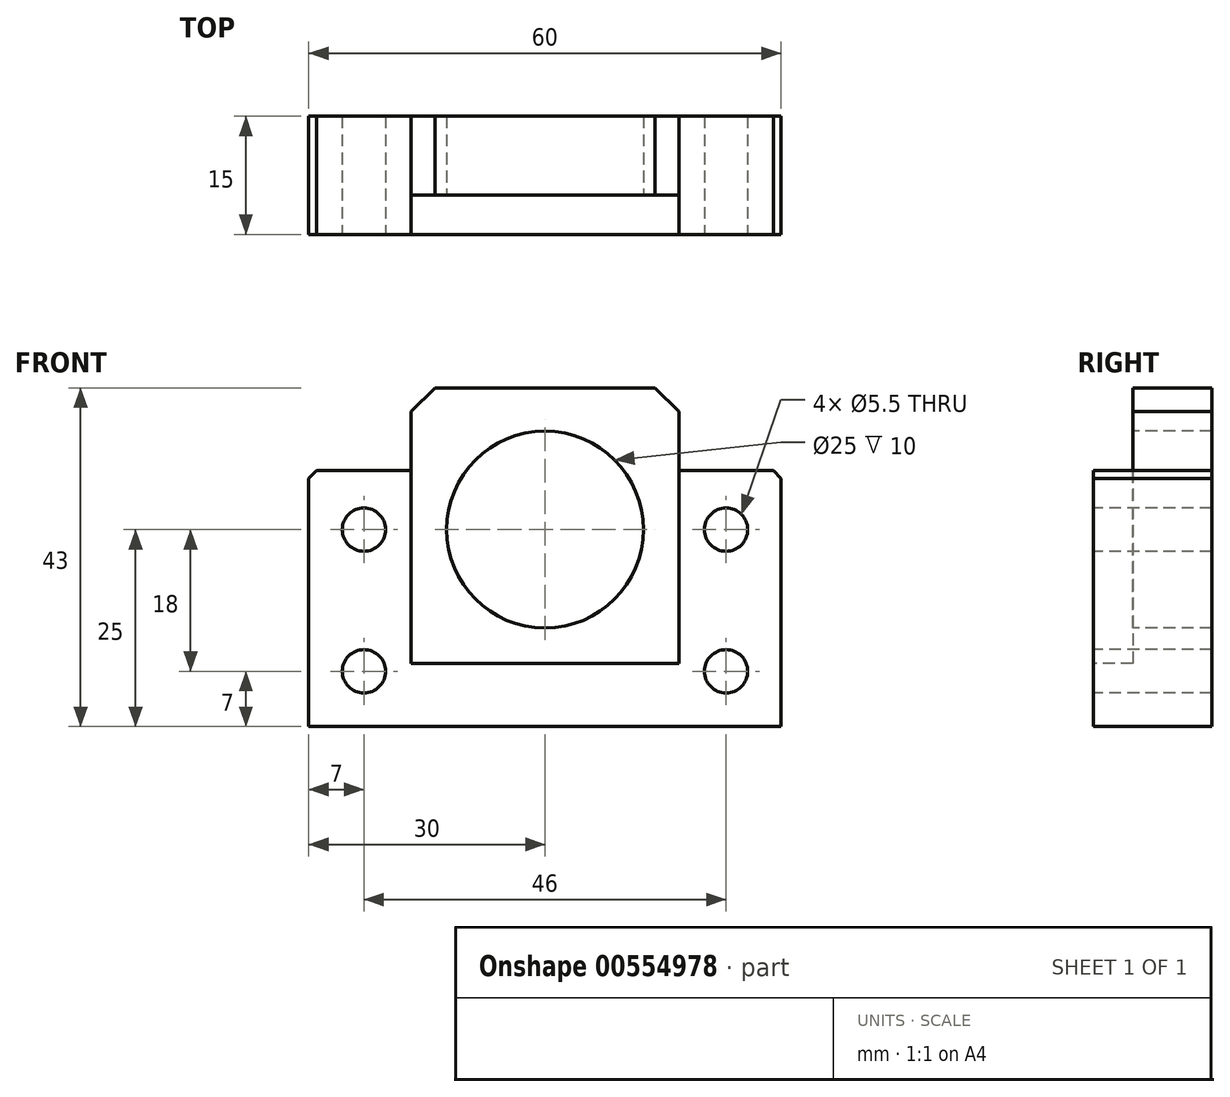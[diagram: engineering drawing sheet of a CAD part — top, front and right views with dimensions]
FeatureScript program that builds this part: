
annotation { "Feature Type Name" : "Feature", "Feature Type Description" : "" }
export const myFeature = defineFeature(function(context is Context, id is Id, definition is map)
    precondition{}
    {
        {
            var Q0;
            Q0=qCreatedBy(makeId("Front.planeOp"),FACE);
            var sketch = newSketch(context, id + "F0", { "sketchPlane" : qUnion([Q0])});
            skLineSegment(sketch, "E0.bottom", {"start": v(17, 21.5) * mm, "end": v(-17, 21.5) * mm});
            skLineSegment(sketch, "E0.top", {"start": v(30, -21.5) * mm, "end": v(-30, -21.5) * mm});
            skLineSegment(sketch, "E0.left", {"start": v(30, 11) * mm, "end": v(30, -21.5) * mm});
            skLineSegment(sketch, "E0.right", {"start": v(-30, 11) * mm, "end": v(-30, -21.5) * mm});
            skPoint(sketch, "E0.middle", {"position": v(0, 0) * mm});
            skLineSegment(sketch, "E1", {"start": v(-17, 21.5) * mm, "end": v(-17, 11) * mm});
            skLineSegment(sketch, "E2", {"start": v(-17, 11) * mm, "end": v(-30, 11) * mm});
            skLineSegment(sketch, "E3", {"start": v(17, 21.5) * mm, "end": v(17, 11) * mm});
            skLineSegment(sketch, "E4", {"start": v(17, 11) * mm, "end": v(30, 11) * mm});
            skPoint(sketch, "E5.orphan", {"position": v(-30, 21.5) * mm});
            skPoint(sketch, "E6.orphan", {"position": v(30, 21.5) * mm});
            skSolve(sketch);
        }
        {
            var Q0;
            Q0=qSketchRegion(id+"F0",true);
            extrude(context, id + "F1", {"entities" : qUnion([Q0]), "endBound" : BoundingType.SYMMETRIC, "depth" : 15 * mm, "offsetDistance" : 25 * mm});
        }
        {
            var Q0;
            Q0=makeQuery(id+"F1.opExtrude","CAP_FACE",FACE,{"disambiguationData":[OSD([sQuery(id+"F0.wireOp",EDGE,"E0.bottom"),sQuery(id+"F0.wireOp",EDGE,"E0.top"),sQuery(id+"F0.wireOp",EDGE,"E0.left"),sQuery(id+"F0.wireOp",EDGE,"E0.right"),sQuery(id+"F0.wireOp",EDGE,"E1"),sQuery(id+"F0.wireOp",EDGE,"E2"),sQuery(id+"F0.wireOp",EDGE,"E3"),sQuery(id+"F0.wireOp",EDGE,"E4")])],"isStart":false});
            var sketch = newSketch(context, id + "F2", { "sketchPlane" : qUnion([Q0])});
            skCircle(sketch, "E7", {"center": v(0, 3.5) * mm, "radius": 12.5 * mm});
            skCircle(sketch, "E8", {"center": v(-23, 3.5) * mm, "radius": 2.75 * mm});
            skCircle(sketch, "E9", {"center": v(23, 3.5) * mm, "radius": 2.75 * mm});
            skCircle(sketch, "E10", {"center": v(-23, -14.5) * mm, "radius": 2.75 * mm});
            skCircle(sketch, "E11", {"center": v(23, -14.5) * mm, "radius": 2.75 * mm});
            skSolve(sketch);
        }
        {
            var Q0;
            Q0=qSketchRegion(id+"F2",true);
            extrude(context, id + "F3", {"entities" : qUnion([Q0]), "operationType" : NewBodyOperationType.REMOVE, "oppositeDirection" : true, "depth" : 15 * mm, "offsetDistance" : 25 * mm});
        }
        {
            var Q0;
            Q0=makeQuery(id+"F1.opExtrude","SWEPT_EDGE",EDGE,{"disambiguationData":[OSD([sQuery(id+"F0.wireOp",EDGE,"E0.bottom"),sQuery(id+"F0.wireOp",EDGE,"E3")])]});
            var Q1;
            Q1=makeQuery(id+"F1.opExtrude","SWEPT_EDGE",EDGE,{"disambiguationData":[OSD([sQuery(id+"F0.wireOp",EDGE,"E0.bottom"),sQuery(id+"F0.wireOp",EDGE,"E1")])]});
            chamfer(context, id + "F4", {"entities" : qUnion([Q0, Q1]), "width" : 3 * mm, "tangentPropagation" : true});
        }
        {
            var Q0;
            Q0=makeQuery(id+"F1.opExtrude","SWEPT_EDGE",EDGE,{"disambiguationData":[OSD([sQuery(id+"F0.wireOp",EDGE,"E0.right"),sQuery(id+"F0.wireOp",EDGE,"E2")])]});
            var Q1;
            Q1=makeQuery(id+"F1.opExtrude","SWEPT_EDGE",EDGE,{"disambiguationData":[OSD([sQuery(id+"F0.wireOp",EDGE,"E0.left"),sQuery(id+"F0.wireOp",EDGE,"E4")])]});
            chamfer(context, id + "F5", {"entities" : qUnion([Q0, Q1]), "width" : 1 * mm, "tangentPropagation" : true});
        }
        {
            var Q0;
            Q0=makeQuery(id+"F1.opExtrude","CAP_FACE",FACE,{"disambiguationData":[OSD([sQuery(id+"F0.wireOp",EDGE,"E0.bottom"),sQuery(id+"F0.wireOp",EDGE,"E0.top"),sQuery(id+"F0.wireOp",EDGE,"E0.left"),sQuery(id+"F0.wireOp",EDGE,"E0.right"),sQuery(id+"F0.wireOp",EDGE,"E1"),sQuery(id+"F0.wireOp",EDGE,"E2"),sQuery(id+"F0.wireOp",EDGE,"E3"),sQuery(id+"F0.wireOp",EDGE,"E4")])],"isStart":false});
            var sketch = newSketch(context, id + "F6", { "sketchPlane" : qUnion([Q0])});
            skLineSegment(sketch, "E12.bottom", {"start": v(17, 20.5) * mm, "end": v(-17, 20.5) * mm});
            skLineSegment(sketch, "E12.top", {"start": v(17, -13.5) * mm, "end": v(-17, -13.5) * mm});
            skLineSegment(sketch, "E12.left", {"start": v(17, 20.5) * mm, "end": v(17, -13.5) * mm});
            skLineSegment(sketch, "E12.right", {"start": v(-17, 20.5) * mm, "end": v(-17, -13.5) * mm});
            skPoint(sketch, "E12.middle", {"position": v(0, 3.5) * mm});
            skLineSegment(sketch, "E13.bottom", {"start": v(-15.5, 20.5) * mm, "end": v(15.5, 20.5) * mm});
            skLineSegment(sketch, "E13.top", {"start": v(-15.5, 28.87) * mm, "end": v(15.5, 28.87) * mm});
            skLineSegment(sketch, "E13.left", {"start": v(-15.5, 20.5) * mm, "end": v(-15.5, 28.87) * mm});
            skLineSegment(sketch, "E13.right", {"start": v(15.5, 20.5) * mm, "end": v(15.5, 28.87) * mm});
            skSolve(sketch);
        }
        {
            var Q0;
            Q0 = qSketchRegion(id + "F6", true);
            extrude(context, id + "F7", {"entities" : qUnion([Q0]), "operationType" : NewBodyOperationType.REMOVE, "oppositeDirection" : true, "depth" : 5 * mm, "offsetDistance" : 25 * mm});
        }
    });
